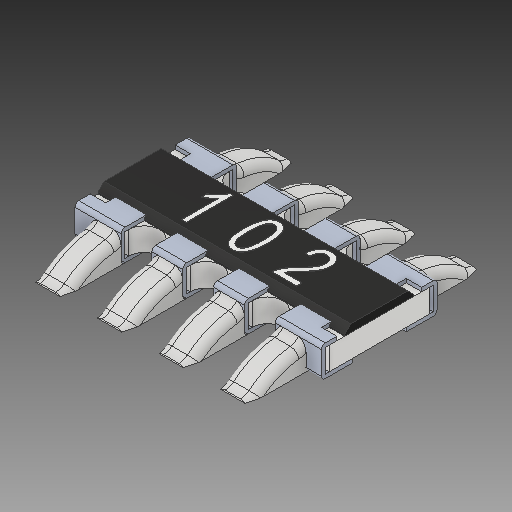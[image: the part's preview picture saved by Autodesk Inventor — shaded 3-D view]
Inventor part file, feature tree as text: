
AUTODESK INVENTOR PART (.ipt)
format: ipt  version: 2019.4 (Build 234330000, 330)  size: 567,296 bytes
history: native  units: mm
features: other x8, fillet x2
ambient origin geometry x8: Origin, YZ Plane, XZ Plane, XY Plane, X Axis, Y Axis, Z Axis, Center Point
bodies: Solid1 (feature_tree), Solid2 (feature_tree), Solid3 (feature_tree), Solid4 (feature_tree), Solid5 (feature_tree), Solid6 (feature_tree), Solid7 (feature_tree), Solid8 (feature_tree), Solid9 (feature_tree), Solid10 (feature_tree)
feature tree (10):
  other  "Cut-Extrude7"
  other  "Boss-Extrude5"
  fillet  "Fillet2"  [1 undecoded]
  fillet  "Fillet1"  [1 undecoded]
  other  "LPattern3[1]"
  other  "LPattern3[2]"
  other  "LPattern3[3]"
  other  "LPattern3[4]"
  other  "LPattern3[5]"
  other  "LPattern3[6]"
note: 2 required parameter values undecoded (feature->parameter linkage not recoverable at this tier; creation-order binding heuristic only, values carry confidence <= 0.55)
